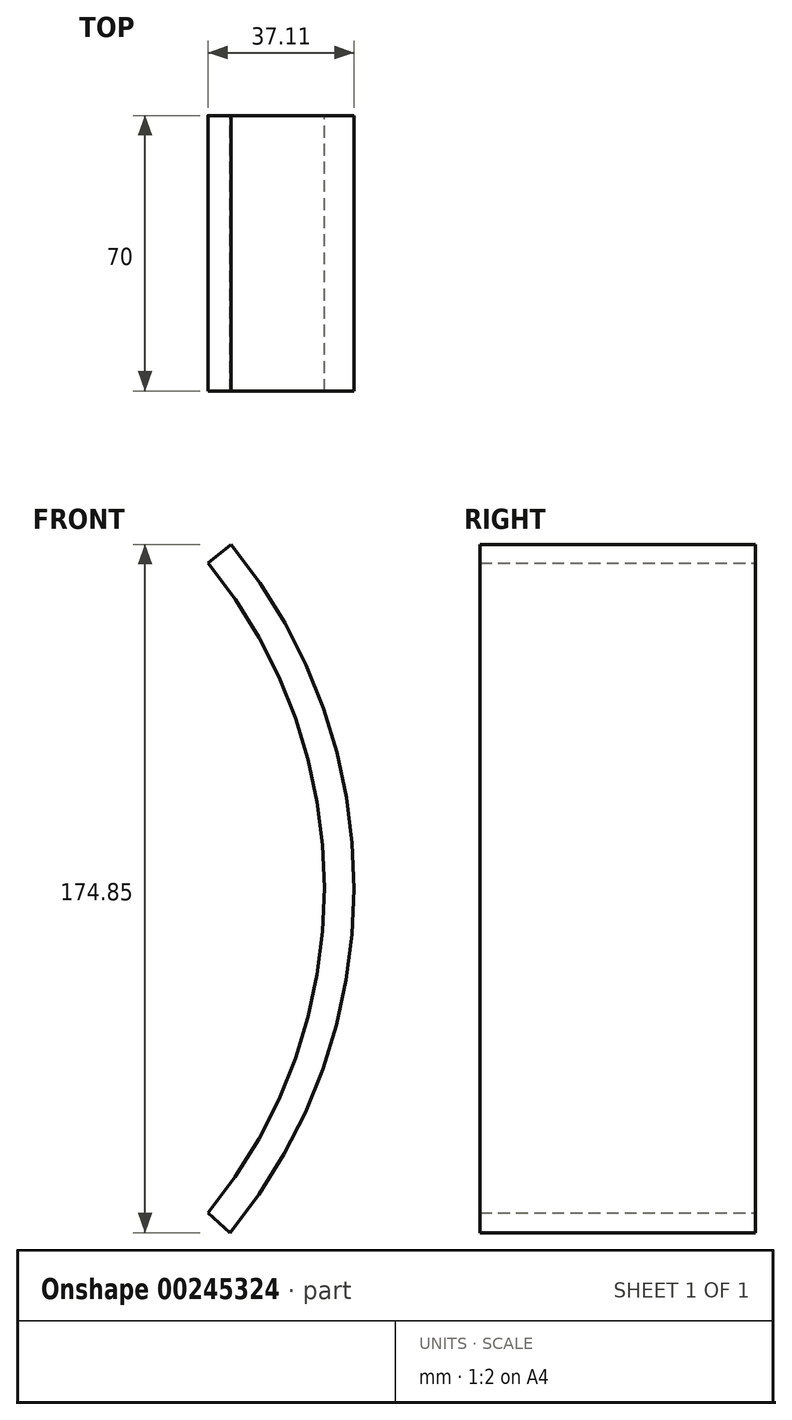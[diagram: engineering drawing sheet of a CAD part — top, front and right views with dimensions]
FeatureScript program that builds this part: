
annotation { "Feature Type Name" : "Feature", "Feature Type Description" : "" }
export const myFeature = defineFeature(function(context is Context, id is Id, definition is map)
    precondition{}
    {
        {
            var Q0;
            Q0=qCreatedBy(makeId("Front.planeOp"),FACE);
            var sketch = newSketch(context, id + "F0", { "sketchPlane" : qUnion([Q0])});
            skArc(sketch, "E0", {"start": v(0, -165.18) * mm, "mid": v(29.6, -82.6) * mm, "end": v(0, 0) * mm});
            skArc(sketch, "E1", {"start": v(5.62, -170.15) * mm, "mid": v(37.1, -82.76) * mm, "end": v(5.84, 4.7) * mm});
            skLineSegment(sketch, "E2", {"start": v(0.05, -0.06) * mm, "end": v(5.84, 4.7) * mm});
            skLineSegment(sketch, "E3", {"start": v(5.84, 4.7) * mm, "end": v(0.05, -0.06) * mm});
            skLineSegment(sketch, "E4", {"start": v(5.62, -170.15) * mm, "end": v(0, -165.18) * mm});
            skSolve(sketch);
        }
        {
            var Q0;
            Q0 = qSketchRegion(id + "F0", true);
            extrude(context, id + "F1", {"entities" : qUnion([Q0]), "depth" : 70 * mm});
        }
    });
